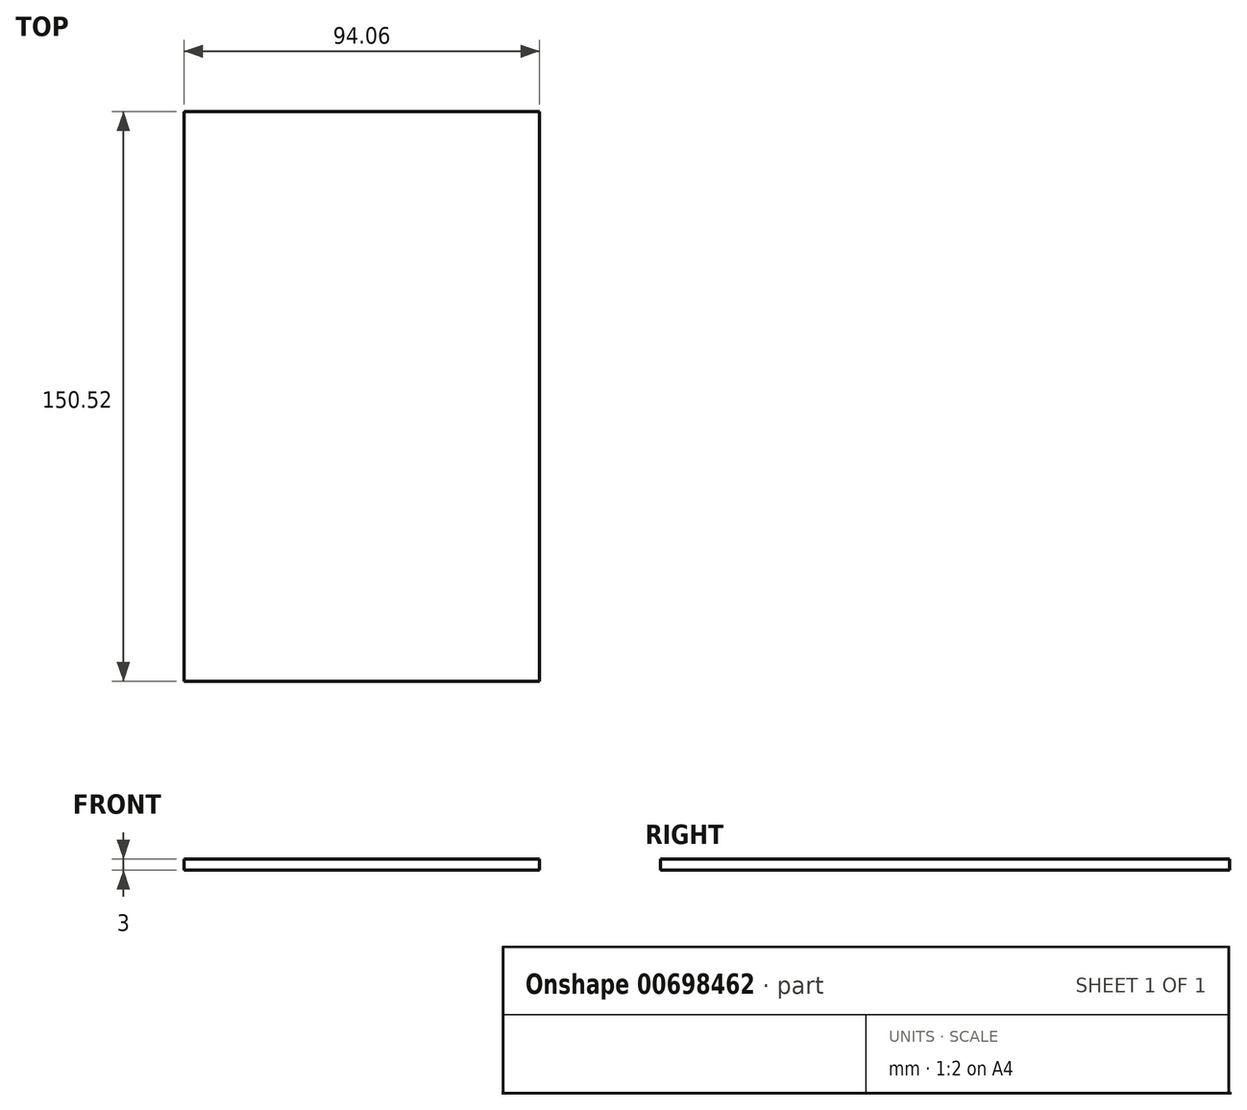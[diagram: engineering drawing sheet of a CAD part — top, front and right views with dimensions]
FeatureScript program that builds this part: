
annotation { "Feature Type Name" : "Feature", "Feature Type Description" : "" }
export const myFeature = defineFeature(function(context is Context, id is Id, definition is map)
    precondition{}
    {
        {
            var Q0;
            Q0=qCreatedBy(makeId("Top.planeOp"),FACE);
            var sketch = newSketch(context, id + "F0", { "sketchPlane" : qUnion([Q0])});
            skLineSegment(sketch, "E0.bottom", {"start": v(47.03, 75.26) * mm, "end": v(-47.03, 75.26) * mm});
            skLineSegment(sketch, "E0.top", {"start": v(47.03, -75.26) * mm, "end": v(-47.03, -75.26) * mm});
            skLineSegment(sketch, "E0.left", {"start": v(47.03, 75.26) * mm, "end": v(47.03, -75.26) * mm});
            skLineSegment(sketch, "E0.right", {"start": v(-47.03, 75.26) * mm, "end": v(-47.03, -75.26) * mm});
            skPoint(sketch, "E0.middle", {"position": v(0, 0) * mm});
            skSolve(sketch);
        }
        {
            var Q0;
            Q0=qSketchRegion(id+"F0",true);
            extrude(context, id + "F1", {"entities" : qUnion([Q0]), "depth" : 3 * mm, "offsetDistance" : 25.4 * mm});
        }
    });
